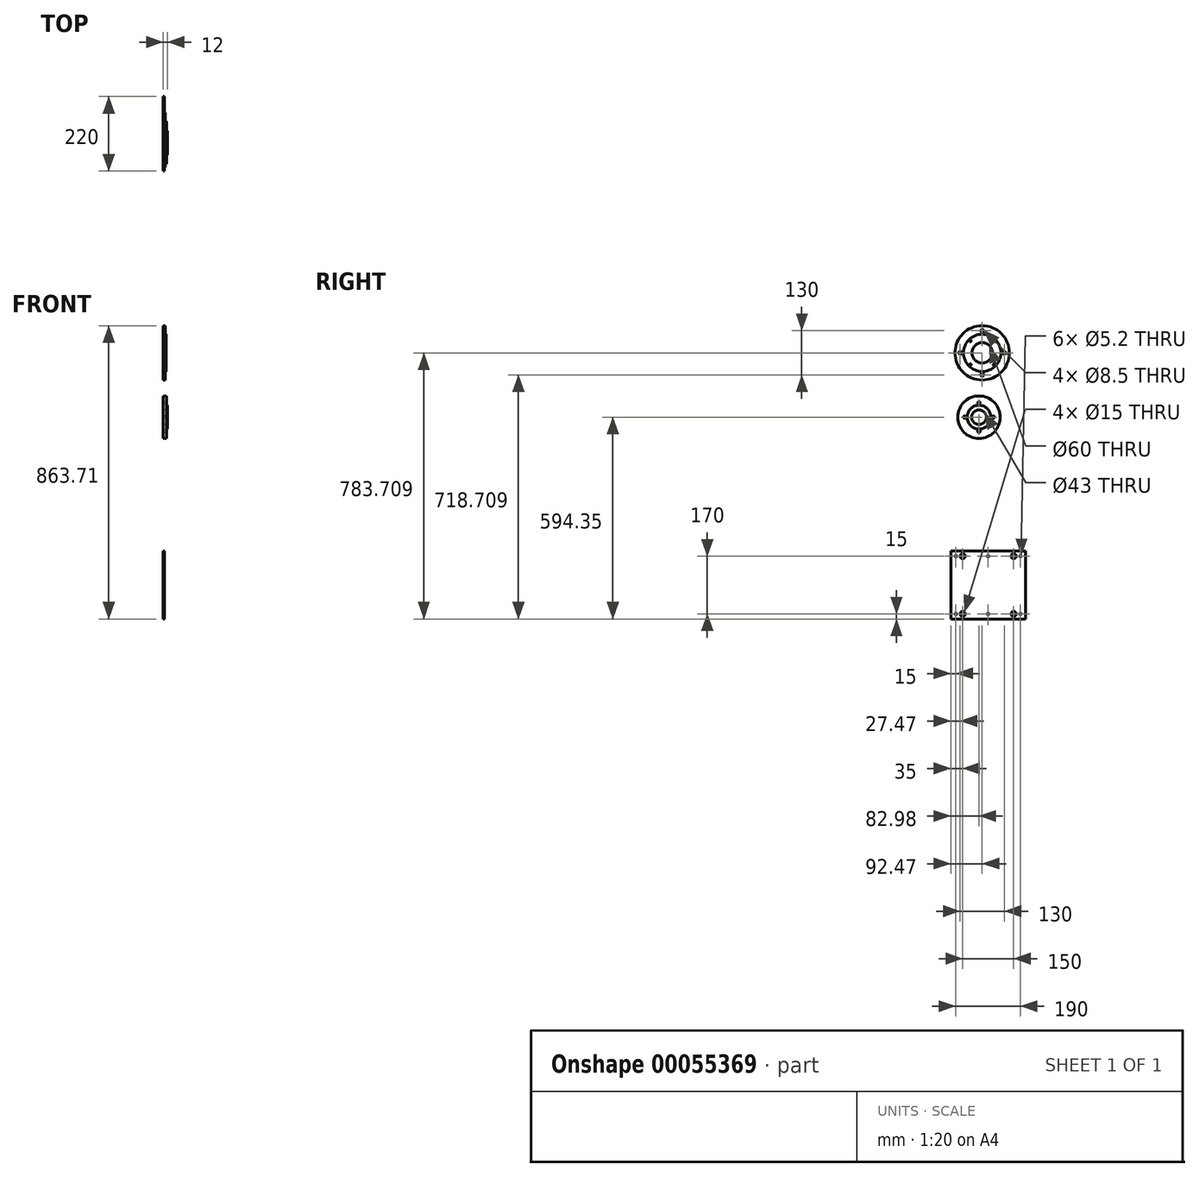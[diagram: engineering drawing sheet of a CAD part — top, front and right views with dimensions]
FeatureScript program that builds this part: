
annotation { "Feature Type Name" : "Feature", "Feature Type Description" : "" }
export const myFeature = defineFeature(function(context is Context, id is Id, definition is map)
    precondition{}
    {
        {
            var Q0;
            Q0=qCreatedBy(makeId("Right.planeOp"),FACE);
            var sketch = newSketch(context, id + "F0", { "sketchPlane" : qUnion([Q0])});
            skCircle(sketch, "E0", {"center": v(0, 0) * mm, "radius": 62.5 * mm});
            skCircle(sketch, "E1", {"center": v(0, 0) * mm, "radius": 21.5 * mm});
            skCircle(sketch, "E2", {"center": v(0, 0) * mm, "radius": 42.3 * mm, "construction": true});
            skLineSegment(sketch, "E3", {"start": v(0, 0) * mm, "end": v(0, 42.3) * mm, "construction": true});
            skCircle(sketch, "E4", {"center": v(0, 42.3) * mm, "radius": 3.4 * mm});
            skCircle(sketch, "E5", {"center": v(0, 0) * mm, "radius": 35 * mm});
            skCircle(sketch, "E6.1.0", {"center": v(-42.3, 0) * mm, "radius": 3.4 * mm});
            skCircle(sketch, "E6.2.0", {"center": v(0, -42.3) * mm, "radius": 3.4 * mm});
            skCircle(sketch, "E6.3.0", {"center": v(42.3, 0) * mm, "radius": 3.4 * mm});
            skSolve(sketch);
        }
        {
            var Q0;
            Q0=makeQuery(id+"F0.imprint","IMPRINT",FACE,{"disambiguationData":[TD([[makeQuery(id+"F0.imprint","IMPRINT",EDGE,{"derivedFrom":sQuery(id+"F0.wireOp",EDGE,"E0")}),1.0]])]});
            extrude(context, id + "F1", {"entities" : qUnion([Q0]), "depth" : 10 * mm});
        }
        {
            var Q0;
            Q0=makeQuery(id+"F0.imprint","IMPRINT",FACE,{"disambiguationData":[TD([[makeQuery(id+"F0.imprint","IMPRINT",EDGE,{"derivedFrom":sQuery(id+"F0.wireOp",EDGE,"E1")}),-1.0]])]});
            extrude(context, id + "F2", {"entities" : qUnion([Q0]), "operationType" : NewBodyOperationType.ADD, "depth" : 12 * mm});
        }
        {
            var Q0;
            Q0=qCreatedBy(makeId("Right.planeOp"),FACE);
            var sketch = newSketch(context, id + "F3", { "sketchPlane" : qUnion([Q0])});
            skCircle(sketch, "E7", {"center": v(9.5, 189.36) * mm, "radius": 30 * mm});
            skCircle(sketch, "E8", {"center": v(9.5, 189.36) * mm, "radius": 80 * mm});
            skLineSegment(sketch, "E9", {"start": v(9.5, 189.36) * mm, "end": v(9.5, 242.73) * mm, "construction": true});
            skLineSegment(sketch, "E10", {"start": v(89.5, 189.36) * mm, "end": v(-56.59, 189.36) * mm, "construction": true});
            skCircle(sketch, "E11", {"center": v(74.5, 189.36) * mm, "radius": 4.25 * mm});
            skCircle(sketch, "E12", {"center": v(9.5, 189.36) * mm, "radius": 65 * mm, "construction": true});
            skCircle(sketch, "E13", {"center": v(9.5, 189.36) * mm, "radius": 49.21 * mm, "construction": true});
            skCircle(sketch, "E14", {"center": v(-25.3, 224.16) * mm, "radius": 2.5 * mm});
            skCircle(sketch, "E15.1.0", {"center": v(9.5, 254.36) * mm, "radius": 4.25 * mm});
            skCircle(sketch, "E15.2.0", {"center": v(-55.5, 189.36) * mm, "radius": 4.25 * mm});
            skCircle(sketch, "E16.1.3.0", {"center": v(9.5, 124.36) * mm, "radius": 4.25 * mm});
            skCircle(sketch, "E17.1.0", {"center": v(-25.3, 154.56) * mm, "radius": 2.5 * mm});
            skCircle(sketch, "E17.2.0", {"center": v(44.3, 154.56) * mm, "radius": 2.5 * mm});
            skCircle(sketch, "E18.1.3.0", {"center": v(44.3, 224.16) * mm, "radius": 2.5 * mm});
            skCircle(sketch, "E19", {"center": v(9.5, 189.36) * mm, "radius": 55 * mm});
            skSolve(sketch);
        }
        {
            var Q0;
            Q0=makeQuery(id+"F3.imprint","IMPRINT",FACE,{"disambiguationData":[TD([[makeQuery(id+"F3.imprint","IMPRINT",EDGE,{"derivedFrom":sQuery(id+"F3.wireOp",EDGE,"E8")}),1.0]])]});
            extrude(context, id + "F4", {"entities" : qUnion([Q0]), "depth" : 6 * mm});
        }
        {
            var Q0;
            Q0=makeQuery(id+"F3.imprint","IMPRINT",FACE,{"disambiguationData":[TD([[makeQuery(id+"F3.imprint","IMPRINT",EDGE,{"derivedFrom":sQuery(id+"F3.wireOp",EDGE,"E7")}),-1.0]])]});
            extrude(context, id + "F5", {"entities" : qUnion([Q0]), "operationType" : NewBodyOperationType.ADD, "depth" : 8 * mm});
        }
        {
            var Q0;
            Q0=qCreatedBy(makeId("Right.planeOp"),FACE);
            var sketch = newSketch(context, id + "F6", { "sketchPlane" : qUnion([Q0])});
            skLineSegment(sketch, "E20.bottom", {"start": v(137.02, -394.35) * mm, "end": v(-82.98, -394.35) * mm});
            skLineSegment(sketch, "E20.top", {"start": v(137.02, -594.35) * mm, "end": v(-82.98, -594.35) * mm});
            skLineSegment(sketch, "E20.left", {"start": v(137.02, -394.35) * mm, "end": v(137.02, -594.35) * mm});
            skLineSegment(sketch, "E20.right", {"start": v(-82.98, -394.35) * mm, "end": v(-82.98, -594.35) * mm});
            skCircle(sketch, "E21", {"center": v(-67.98, -409.35) * mm, "radius": 2.6 * mm});
            skCircle(sketch, "E22", {"center": v(-47.98, -409.35) * mm, "radius": 7.5 * mm});
            skCircle(sketch, "E23.0.1.0", {"center": v(-47.98, -579.35) * mm, "radius": 7.5 * mm});
            skCircle(sketch, "E23.1.0.0", {"center": v(102.02, -409.35) * mm, "radius": 7.5 * mm});
            skCircle(sketch, "E23.1.1.0", {"center": v(102.02, -579.35) * mm, "radius": 7.5 * mm});
            skLineSegment(sketch, "E23.direction1", {"start": v(-47.98, -409.35) * mm, "end": v(102.02, -409.35) * mm, "construction": true});
            skLineSegment(sketch, "E23.direction2", {"start": v(-47.98, -409.35) * mm, "end": v(-47.98, -579.35) * mm, "construction": true});
            skCircle(sketch, "E24.0.1.0", {"center": v(-67.98, -579.35) * mm, "radius": 2.6 * mm});
            skCircle(sketch, "E24.1.0.0", {"center": v(27.02, -409.35) * mm, "radius": 2.6 * mm});
            skCircle(sketch, "E24.1.1.0", {"center": v(27.02, -579.35) * mm, "radius": 2.6 * mm});
            skCircle(sketch, "E24.2.0.0", {"center": v(122.02, -409.35) * mm, "radius": 2.6 * mm});
            skCircle(sketch, "E24.2.1.0", {"center": v(122.02, -579.35) * mm, "radius": 2.6 * mm});
            skLineSegment(sketch, "E24.direction1", {"start": v(-67.98, -409.35) * mm, "end": v(27.02, -409.35) * mm, "construction": true});
            skLineSegment(sketch, "E24.direction2", {"start": v(-67.98, -409.35) * mm, "end": v(-67.98, -579.35) * mm, "construction": true});
            skSolve(sketch);
        }
        {
            var Q0;
            Q0=makeQuery(id+"F6.imprint","IMPRINT",FACE,{"disambiguationData":[TD([[makeQuery(id+"F6.imprint","IMPRINT",EDGE,{"derivedFrom":sQuery(id+"F6.wireOp",EDGE,"E20.bottom")}),1.0]])]});
            extrude(context, id + "F7", {"entities" : qUnion([Q0]), "depth" : 4 * mm});
        }
    });
